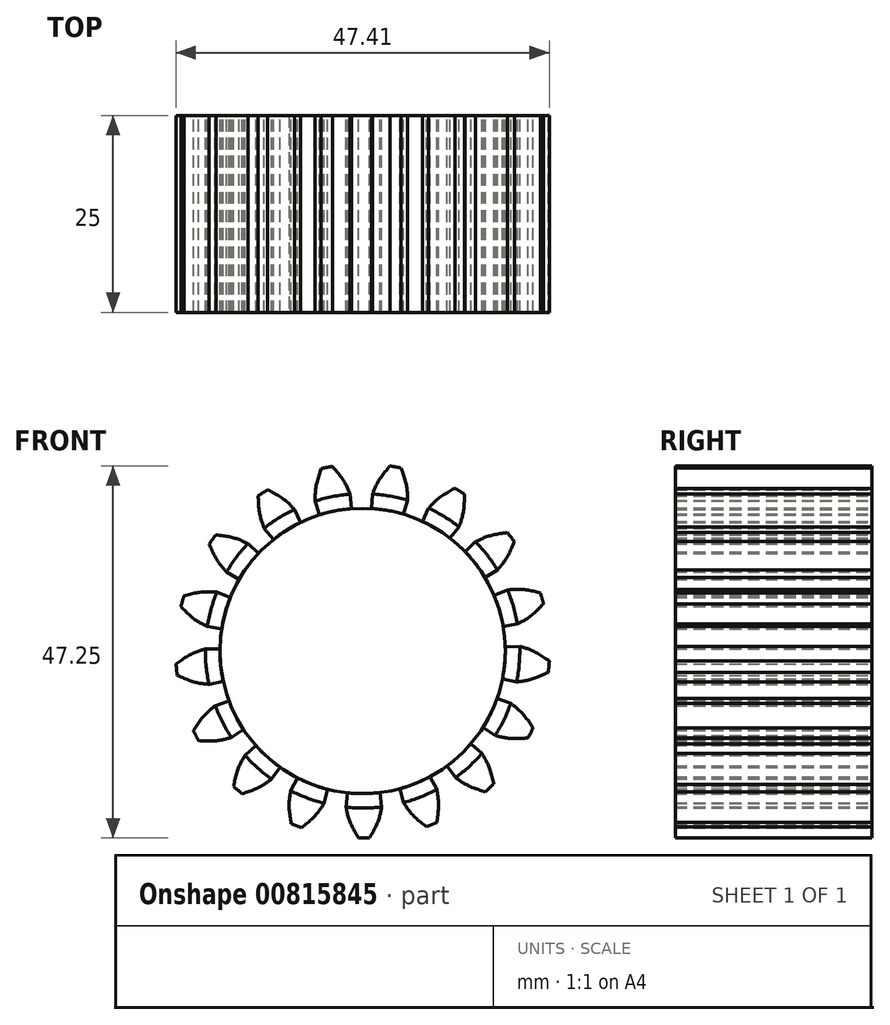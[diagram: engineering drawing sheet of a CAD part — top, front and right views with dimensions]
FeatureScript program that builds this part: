
annotation { "Feature Type Name" : "Feature", "Feature Type Description" : "" }
export const myFeature = defineFeature(function(context is Context, id is Id, definition is map)
    precondition{}
    {
        {
            var Q0;
            Q0=qCreatedBy(makeId("Front.planeOp"),FACE);
            var sketch = newSketch(context, id + "F0", { "sketchPlane" : qUnion([Q0])});
            skCircle(sketch, "E0", {"center": v(0, 0) * mm, "radius": 21.25 * mm, "construction": true});
            skCircle(sketch, "E1.0", {"center": v(0, 0) * mm, "radius": 23.75 * mm});
            skCircle(sketch, "E2.0", {"center": v(0, 0) * mm, "radius": 18.13 * mm});
            skArc(sketch, "E3", {"start": v(6.83, 18.76) * mm, "mid": v(3.68, 19.63) * mm, "end": v(0.42, 19.96) * mm});
            skLineSegment(sketch, "E4", {"start": v(-5.25, 23.16) * mm, "end": v(6.83, 18.76) * mm, "construction": true});
            skPoint(sketch, "E5.orphan", {"position": v(0, 21.25) * mm});
            skLineSegment(sketch, "E6", {"start": v(6.83, 18.76) * mm, "end": v(0, 0) * mm, "construction": true});
            skPoint(sketch, "E7", {"position": v(-6.03, 19.04) * mm});
            skLineSegment(sketch, "E8", {"start": v(-6.03, 19.04) * mm, "end": v(0, 0) * mm});
            skLineSegment(sketch, "E9", {"start": v(0, 0) * mm, "end": v(3.68, 19.63) * mm, "construction": true});
            skLineSegment(sketch, "E10", {"start": v(0, 0) * mm, "end": v(0.42, 19.96) * mm, "construction": true});
            skLineSegment(sketch, "E11", {"start": v(0, 0) * mm, "end": v(-2.84, 19.77) * mm, "construction": true});
            skLineSegment(sketch, "E12", {"start": v(3.68, 19.63) * mm, "end": v(-5.8, 21.4) * mm, "construction": true});
            skLineSegment(sketch, "E13", {"start": v(0.42, 19.96) * mm, "end": v(-6, 20.1) * mm, "construction": true});
            skLineSegment(sketch, "E14", {"start": v(-2.84, 19.77) * mm, "end": v(-6.02, 19.3) * mm, "construction": true});
            skFitSpline(sketch, "E15", {"points": [v(-5.25, 23.16) * mm, v(-5.8, 21.4) * mm, v(-6, 20.1) * mm, v(-6.02, 19.3) * mm, v(-6.03, 19.04) * mm], "startDerivative": vector(-1.8, -5.21) * mm, "endDerivative": vector(-0.05, -1.79) * mm});
            skPoint(sketch, "E16", {"position": v(-5.98, 20.4) * mm});
            skLineSegment(sketch, "E17", {"start": v(0, 0) * mm, "end": v(-6.22, 31.87) * mm, "construction": true});
            skFitSpline(sketch, "E18.MirrorCS", {"points": [v(-3.84, 23.44) * mm, v(-2.67, 22.01) * mm, v(-2, 20.88) * mm, v(-1.68, 20.16) * mm, v(-1.58, 19.9) * mm], "startDerivative": vector(3.62, -4.16) * mm, "endDerivative": vector(0.72, -1.64) * mm});
            skLineSegment(sketch, "E19", {"start": v(-5.98, 20.4) * mm, "end": v(0, 0) * mm, "construction": true});
            skArc(sketch, "E20.trimOffspring", {"start": v(-1.58, 19.9) * mm, "mid": v(-3.83, 19.6) * mm, "end": v(-6.03, 19.04) * mm});
            skLineSegment(sketch, "E21", {"start": v(-1.58, 19.9) * mm, "end": v(0, 0) * mm});
            skSolve(sketch);
        }
        {
            var Q0;
            {var subQ0=sQuery(id+"F0.wireOp",EDGE,"E18.MirrorCS");Q0=makeQuery(id+"F0.imprint","IMPRINT",FACE,{"disambiguationData":[TD([[makeQuery(id+"F0.imprint","IMPRINT",EDGE,{"derivedFrom":subQ0}),-1.0]])]});}
            var Q1;
            {var subQ1=sQuery(id+"F0.wireOp",EDGE,"E15");var subQ5=sQuery(id+"F0.wireOp",EDGE,"E1.0");var subQ6=makeQuery(id+"F0.imprint","INTERSECT",VERTEX,{"derivedFrom":[subQ5,subQ1]});Q1=makeQuery(id+"F0.imprint","IMPRINT",FACE,{"disambiguationData":[TD([[makeQuery(id+"F0.imprint","IMPRINT",EDGE,{"disambiguationData":[TD([[subQ6,1.0]])],"derivedFrom":subQ5}),1.0]])]});}
            var Q2;
            {var subQ0=sQuery(id+"F0.wireOp",EDGE,"E20.trimOffspring");var subQ1=sQuery(id+"F0.wireOp",EDGE,"E15");var subQ2=makeQuery(id+"F0.imprint","INTERSECT",VERTEX,{"derivedFrom":[subQ1,subQ0]});Q2=makeQuery(id+"F0.imprint","IMPRINT",FACE,{"disambiguationData":[TD([[makeQuery(id+"F0.imprint","IMPRINT",EDGE,{"disambiguationData":[TD([[subQ2,1.0]])],"derivedFrom":subQ1}),1.0]])]});}
            extrude(context, id + "F1", {"entities" : qUnion([Q0, Q1, Q2]), "depth" : 25 * mm, "offsetDistance" : 25 * mm});
        }
        {
            var Q0;
            Q0=qCreatedBy(makeId("Right.planeOp"),FACE);
            var sketch = newSketch(context, id + "F2", { "sketchPlane" : qUnion([Q0])});
            skLineSegment(sketch, "E22", {"start": v(0, 0) * mm, "end": v(-38.13, 0) * mm});
            skSolve(sketch);
        }
        {
            var Q0;
            Q0=makeQuery(id+"F1.opExtrude","SWEPT_BODY",BODY,{"disambiguationData":[OSD([sQuery(id+"F0.wireOp",EDGE,"E1.0"),sQuery(id+"F0.wireOp",EDGE,"E15"),sQuery(id+"F0.wireOp",EDGE,"E18.MirrorCS"),sQuery(id+"F0.wireOp",EDGE,"E20.trimOffspring")])]});
            var Q1;
            Q1=sQuery(id+"F2.wireOp",EDGE,"E22");
            circularPattern(context, id + "F3", {"entities" : qUnion([Q0]), "axis" : qUnion([Q1]), "angle" : 360 * degree, "instanceCount" : 17, "equalSpace" : true});
        }
        {
            var Q0;
            {var subQ0=sQuery(id+"F0.wireOp",EDGE,"E8");var subQ1=sQuery(id+"F0.wireOp",EDGE,"E2.0");var subQ2=makeQuery(id+"F0.imprint","INTERSECT",VERTEX,{"derivedFrom":[subQ1,subQ0]});Q0=makeQuery(id+"F0.imprint","IMPRINT",FACE,{"disambiguationData":[TD([[makeQuery(id+"F0.imprint","IMPRINT",EDGE,{"disambiguationData":[TD([[subQ2,-1.0]])],"derivedFrom":subQ1}),1.0]])]});}
            var Q1;
            {var subQ0=sQuery(id+"F0.wireOp",EDGE,"E8");var subQ1=sQuery(id+"F0.wireOp",EDGE,"E2.0");var subQ2=makeQuery(id+"F0.imprint","INTERSECT",VERTEX,{"derivedFrom":[subQ1,subQ0]});Q1=makeQuery(id+"F0.imprint","IMPRINT",FACE,{"disambiguationData":[TD([[makeQuery(id+"F0.imprint","IMPRINT",EDGE,{"disambiguationData":[TD([[subQ2,1.0]])],"derivedFrom":subQ1}),1.0]])]});}
            extrude(context, id + "F4", {"entities" : qUnion([Q0, Q1]), "depth" : 25 * mm, "offsetDistance" : 25 * mm});
        }
        {
            var Q0;
            {var subQ5=sQuery(id+"F0.wireOp",EDGE,"E20.trimOffspring");Q0=makeQuery(id+"F0.imprint","IMPRINT",FACE,{"disambiguationData":[TD([[makeQuery(id+"F0.imprint","IMPRINT",EDGE,{"derivedFrom":subQ5}),1.0]])]});}
            extrude(context, id + "F5", {"entities" : qUnion([Q0]), "depth" : 25 * mm, "offsetDistance" : 25 * mm});
        }
        {
            var Q0;
            Q0=makeQuery(id+"F5.opExtrude","SWEPT_BODY",BODY,{"disambiguationData":[OSD([sQuery(id+"F0.wireOp",EDGE,"E2.0"),sQuery(id+"F0.wireOp",EDGE,"E8"),sQuery(id+"F0.wireOp",EDGE,"E20.trimOffspring"),sQuery(id+"F0.wireOp",EDGE,"E21")])]});
            var Q1;
            Q1=sQuery(id+"F2.wireOp",EDGE,"E22");
            circularPattern(context, id + "F6", {"entities" : qUnion([Q0]), "axis" : qUnion([Q1]), "angle" : 360 * degree, "instanceCount" : 17, "equalSpace" : true});
        }
    });
